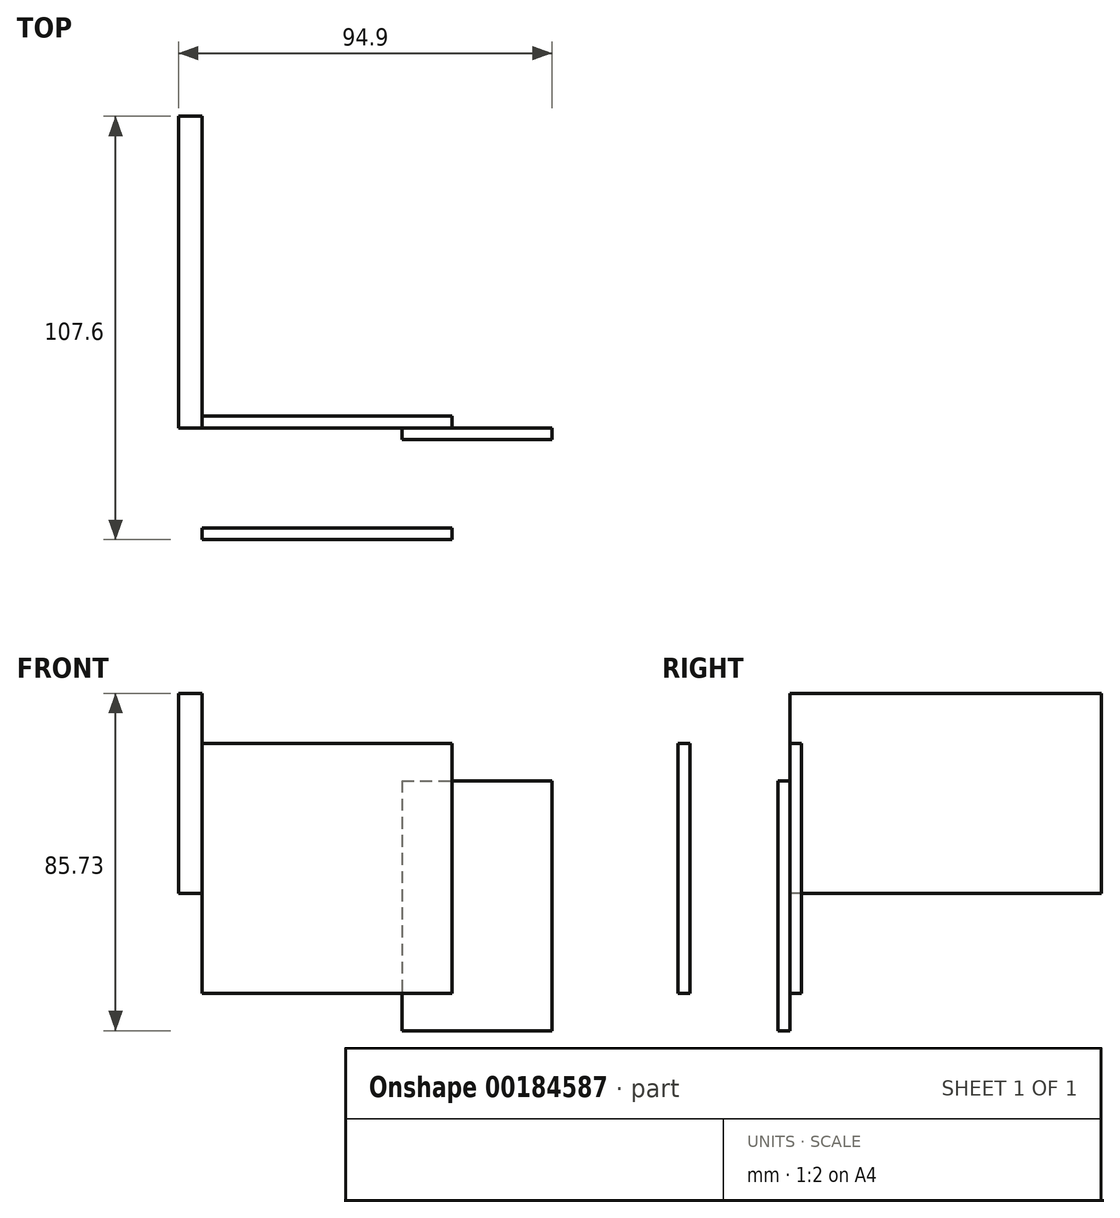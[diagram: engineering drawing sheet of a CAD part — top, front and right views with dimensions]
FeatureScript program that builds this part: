
annotation { "Feature Type Name" : "Feature", "Feature Type Description" : "" }
export const myFeature = defineFeature(function(context is Context, id is Id, definition is map)
    precondition{}
    {
        {
            var Q0;
            Q0=qCreatedBy(makeId("Top.planeOp"),FACE);
            var sketch = newSketch(context, id + "F0", { "sketchPlane" : qUnion([Q0])});
            skLineSegment(sketch, "E0.bottom", {"start": v(0, 0) * mm, "end": v(-63.5, 0) * mm});
            skLineSegment(sketch, "E0.top", {"start": v(0, -3) * mm, "end": v(-63.5, -3) * mm});
            skLineSegment(sketch, "E0.left", {"start": v(0, 0) * mm, "end": v(0, -3) * mm});
            skLineSegment(sketch, "E0.right", {"start": v(-63.5, 0) * mm, "end": v(-63.5, -3) * mm});
            skLineSegment(sketch, "E1.bottom", {"start": v(0, 0) * mm, "end": v(-6, 0) * mm});
            skLineSegment(sketch, "E1.top", {"start": v(0, 76.2) * mm, "end": v(-6, 76.2) * mm});
            skLineSegment(sketch, "E1.left", {"start": v(0, 0) * mm, "end": v(0, 76.2) * mm});
            skLineSegment(sketch, "E1.right", {"start": v(-6, 0) * mm, "end": v(-6, 76.2) * mm});
            skLineSegment(sketch, "E2.bottom", {"start": v(-63.5, -3) * mm, "end": v(-69.5, -3) * mm});
            skLineSegment(sketch, "E2.top", {"start": v(-63.5, 76.2) * mm, "end": v(-69.5, 76.2) * mm});
            skLineSegment(sketch, "E2.left", {"start": v(-63.5, -3) * mm, "end": v(-63.5, 76.2) * mm});
            skLineSegment(sketch, "E2.right", {"start": v(-69.5, -3) * mm, "end": v(-69.5, 76.2) * mm});
            skSolve(sketch);
        }
        {
            var Q0;
            {var subQ3=sQuery(id+"F0.wireOp",EDGE,"E2.bottom");Q0=makeQuery(id+"F0.imprint","IMPRINT",FACE,{"disambiguationData":[TD([[makeQuery(id+"F0.imprint","IMPRINT",EDGE,{"derivedFrom":subQ3}),-1.0]])]});}
            var Q1;
            Q1=makeQuery(id+"F0.imprint","IMPRINT",FACE,{"disambiguationData":[TD([[makeQuery(id+"F0.imprint","IMPRINT",EDGE,{"derivedFrom":sQuery(id+"F0.wireOp",EDGE,"E1.bottom")}),-1.0]])]});
            extrude(context, id + "F1", {"entities" : qUnion([Q0, Q1]), "depth" : 76.2 * mm, "hasSecondDirection" : true, "secondDirectionOppositeDirection" : false, "secondDirectionDepth" : 25.4 * mm});
        }
        {
            var Q0;
            {var subQ1=sQuery(id+"F0.wireOp",EDGE,"E0.bottom");Q0=makeQuery(id+"F0.imprint","IMPRINT",FACE,{"disambiguationData":[TD([[makeQuery(id+"F0.imprint","IMPRINT",EDGE,{"derivedFrom":subQ1}),1.0]])]});}
            extrude(context, id + "F2", {"entities" : qUnion([Q0]), "depth" : 63.5 * mm});
        }
        {
            var Q0;
            Q0=makeQuery(id+"F2.opExtrude","SWEPT_FACE",FACE,{"disambiguationData":[OSD([sQuery(id+"F0.wireOp",EDGE,"E0.top")])]});
            var sketch = newSketch(context, id + "F3", { "sketchPlane" : qUnion([Q0])});
            skLineSegment(sketch, "E3.bottom", {"start": v(-12.7, 53.98) * mm, "end": v(25.4, 53.98) * mm});
            skLineSegment(sketch, "E3.top", {"start": v(-12.7, -9.52) * mm, "end": v(25.4, -9.52) * mm});
            skLineSegment(sketch, "E3.left", {"start": v(-12.7, 53.98) * mm, "end": v(-12.7, -9.52) * mm});
            skLineSegment(sketch, "E3.right", {"start": v(25.4, 53.98) * mm, "end": v(25.4, -9.52) * mm});
            skSolve(sketch);
        }
        {
            var Q0;
            Q0 = qSketchRegion(id + "F3", true);
            extrude(context, id + "F4", {"entities" : qUnion([Q0]), "depth" : 3 * mm});
        }
        {
            var Q0;
            Q0=makeQuery(id+"F2.opExtrude","SWEPT_FACE",FACE,{"disambiguationData":[OSD([sQuery(id+"F0.wireOp",EDGE,"E0.top")])]});
            extrude(context, id + "F5", {"entities" : qUnion([Q0]), "depth" : 25.4 * mm + 3 * mm, "hasSecondDirection" : true, "secondDirectionOppositeDirection" : false, "secondDirectionDepth" : 25.4 * mm});
        }
    });
